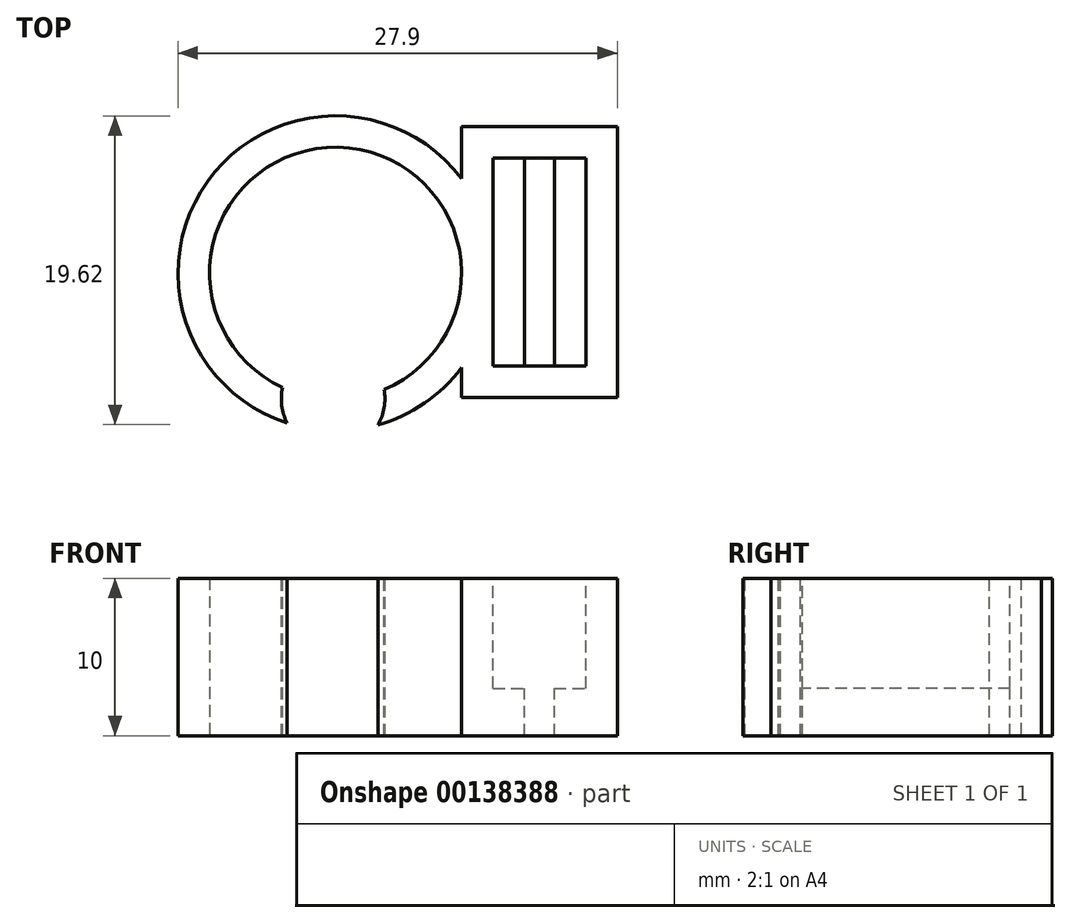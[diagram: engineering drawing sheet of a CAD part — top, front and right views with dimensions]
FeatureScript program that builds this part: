
annotation { "Feature Type Name" : "Feature", "Feature Type Description" : "" }
export const myFeature = defineFeature(function(context is Context, id is Id, definition is map)
    precondition{}
    {
        {
            var Q0;
            Q0=qCreatedBy(makeId("Top.planeOp"),FACE);
            var sketch = newSketch(context, id + "F0", { "sketchPlane" : qUnion([Q0])});
            skCircle(sketch, "E0", {"center": v(-52.4, 40.08) * mm, "radius": 8 * mm});
            skCircle(sketch, "E1", {"center": v(-52.4, 40.08) * mm, "radius": 10 * mm});
            skSolve(sketch);
        }
        {
            var Q0;
            Q0=makeQuery(id+"F0.imprint","IMPRINT",FACE,{"disambiguationData":[TD([[makeQuery(id+"F0.imprint","IMPRINT",EDGE,{"derivedFrom":sQuery(id+"F0.wireOp",EDGE,"E0")}),-1.0]])]});
            extrude(context, id + "F1", {"entities" : qUnion([Q0]), "depth" : 10 * mm});
        }
        {
            var Q0;
            Q0=makeQuery(id+"F1.opExtrude","CAP_FACE",FACE,{"disambiguationData":[OSD([sQuery(id+"F0.wireOp",EDGE,"E0"),sQuery(id+"F0.wireOp",EDGE,"E1")])],"isStart":false});
            var sketch = newSketch(context, id + "F2", { "sketchPlane" : qUnion([Q0])});
            skCircle(sketch, "E2", {"center": v(-52.56, 32.08) * mm, "radius": 3.29 * mm});
            skSolve(sketch);
        }
        {
            var Q0;
            {var subQ0=sQuery(id+"F2.wireOp",EDGE,"E2");var subQ1=makeQuery(id+"F1.opExtrude","CAP_EDGE",EDGE,{"disambiguationData":[OSD([sQuery(id+"F0.wireOp",EDGE,"E1")])],"isStart":false});var subQ2=makeQuery(id+"F2.imprint","INTERSECT",VERTEX,{"disambiguationData":[OD(0.0)],"derivedFrom":[subQ1,subQ0]});Q0=makeQuery(id+"F2.imprint","IMPRINT",FACE,{"disambiguationData":[TD([[makeQuery(id+"F2.imprint","IMPRINT",EDGE,{"disambiguationData":[TD([[subQ2,1.0]])],"derivedFrom":subQ0}),1.0]])]});}
            extrude(context, id + "F3", {"entities" : qUnion([Q0]), "operationType" : NewBodyOperationType.REMOVE, "endBound" : BoundingType.THROUGH_ALL, "oppositeDirection" : true, "depth" : 25 * mm});
        }
        {
            var Q0;
            Q0=makeQuery(id+"F1.opExtrude","CAP_FACE",FACE,{"disambiguationData":[OSD([sQuery(id+"F0.wireOp",EDGE,"E0"),sQuery(id+"F0.wireOp",EDGE,"E1")])],"isStart":false});
            var sketch = newSketch(context, id + "F4", { "sketchPlane" : qUnion([Q0])});
            skLineSegment(sketch, "E3.bottom", {"start": v(-44.4, 49.4) * mm, "end": v(-34.5, 49.4) * mm});
            skLineSegment(sketch, "E3.top", {"start": v(-44.4, 32.2) * mm, "end": v(-34.5, 32.2) * mm});
            skLineSegment(sketch, "E3.left", {"start": v(-44.4, 49.4) * mm, "end": v(-44.4, 32.2) * mm});
            skLineSegment(sketch, "E3.right", {"start": v(-34.5, 49.4) * mm, "end": v(-34.5, 32.2) * mm});
            skSolve(sketch);
        }
        {
            var Q0;
            {var subQ0=sQuery(id+"F4.wireOp",EDGE,"E3.left");var subQ1=makeQuery(id+"F1.opExtrude","CAP_EDGE",EDGE,{"disambiguationData":[OSD([sQuery(id+"F0.wireOp",EDGE,"E1")])],"isStart":false});var subQ2=makeQuery(id+"F4.imprint","INTERSECT",VERTEX,{"disambiguationData":[OD(0.0)],"derivedFrom":[subQ1,subQ0]});Q0=makeQuery(id+"F4.imprint","IMPRINT",FACE,{"disambiguationData":[TD([[makeQuery(id+"F4.imprint","IMPRINT",EDGE,{"disambiguationData":[TD([[subQ2,-1.0]])],"derivedFrom":subQ0}),1.0]])]});}
            extrude(context, id + "F5", {"entities" : qUnion([Q0]), "operationType" : NewBodyOperationType.REMOVE, "endBound" : BoundingType.THROUGH_ALL, "oppositeDirection" : true, "depth" : 25 * mm});
        }
        {
            var Q0;
            Q0 = qSketchRegion(id + "F4", true);
            extrude(context, id + "F6", {"entities" : qUnion([Q0]), "oppositeDirection" : true, "depth" : 7 * mm});
        }
        {
            var Q0;
            Q0=makeQuery(id+"F6.opExtrude","CAP_FACE",FACE,{"disambiguationData":[OSD([sQuery(id+"F4.wireOp",EDGE,"E3.bottom"),sQuery(id+"F4.wireOp",EDGE,"E3.top"),sQuery(id+"F4.wireOp",EDGE,"E3.left"),sQuery(id+"F4.wireOp",EDGE,"E3.right")])],"isStart":true});
            var sketch = newSketch(context, id + "F7", { "sketchPlane" : qUnion([Q0])});
            skLineSegment(sketch, "E4.bottom", {"start": v(-42.4, 47.4) * mm, "end": v(-36.5, 47.4) * mm});
            skLineSegment(sketch, "E4.top", {"start": v(-42.4, 34.2) * mm, "end": v(-36.5, 34.2) * mm});
            skLineSegment(sketch, "E4.left", {"start": v(-42.4, 47.4) * mm, "end": v(-42.4, 34.2) * mm});
            skLineSegment(sketch, "E4.right", {"start": v(-36.5, 47.4) * mm, "end": v(-36.5, 34.2) * mm});
            skSolve(sketch);
        }
        {
            var Q0;
            Q0=makeQuery(id+"F7.imprint","IMPRINT",FACE,{"disambiguationData":[TD([[makeQuery(id+"F7.imprint","IMPRINT",EDGE,{"derivedFrom":sQuery(id+"F7.wireOp",EDGE,"E4.bottom")}),-1.0]])]});
            var Q1;
            Q1 = qSketchRegion(id + "F9", true);
            extrude(context, id + "F8", {"entities" : qUnion([Q0, Q1]), "operationType" : NewBodyOperationType.REMOVE, "oppositeDirection" : true, "depth" : 25 * mm});
        }
        {
            var Q0;
            Q0=makeQuery(id+"F6.opExtrude","CAP_FACE",FACE,{"disambiguationData":[OSD([sQuery(id+"F4.wireOp",EDGE,"E3.bottom"),sQuery(id+"F4.wireOp",EDGE,"E3.top"),sQuery(id+"F4.wireOp",EDGE,"E3.left"),sQuery(id+"F4.wireOp",EDGE,"E3.right")])],"isStart":false});
            var sketch = newSketch(context, id + "F9", { "sketchPlane" : qUnion([Q0])});
            skLineSegment(sketch, "E5.bottom", {"start": v(-42.4, -34.2) * mm, "end": v(-40.4, -34.2) * mm});
            skLineSegment(sketch, "E5.top", {"start": v(-42.4, -47.4) * mm, "end": v(-40.4, -47.4) * mm});
            skLineSegment(sketch, "E5.left", {"start": v(-42.4, -34.2) * mm, "end": v(-42.4, -47.4) * mm});
            skLineSegment(sketch, "E5.right", {"start": v(-40.4, -34.2) * mm, "end": v(-40.4, -47.4) * mm});
            skLineSegment(sketch, "E6.bottom", {"start": v(-38.5, -34.2) * mm, "end": v(-36.5, -34.2) * mm});
            skLineSegment(sketch, "E6.top", {"start": v(-38.5, -47.4) * mm, "end": v(-36.5, -47.4) * mm});
            skLineSegment(sketch, "E6.left", {"start": v(-38.5, -34.2) * mm, "end": v(-38.5, -47.4) * mm});
            skLineSegment(sketch, "E6.right", {"start": v(-36.5, -34.2) * mm, "end": v(-36.5, -47.4) * mm});
            skLineSegment(sketch, "E7.bottom", {"start": v(-44.4, -32.2) * mm, "end": v(-34.5, -32.2) * mm});
            skLineSegment(sketch, "E7.top", {"start": v(-44.4, -49.4) * mm, "end": v(-34.5, -49.4) * mm});
            skLineSegment(sketch, "E7.left", {"start": v(-44.4, -32.2) * mm, "end": v(-44.4, -49.4) * mm});
            skLineSegment(sketch, "E7.right", {"start": v(-34.5, -32.2) * mm, "end": v(-34.5, -49.4) * mm});
            skSolve(sketch);
        }
        {
            var Q0;
            {var subQ1=sQuery(id+"F9.wireOp",EDGE,"E5.bottom");Q0=makeQuery(id+"F9.imprint","IMPRINT",FACE,{"disambiguationData":[TD([[makeQuery(id+"F9.imprint","IMPRINT",EDGE,{"derivedFrom":subQ1}),1.0]])]});}
            var Q1;
            Q1=makeQuery(id+"F9.imprint","IMPRINT",FACE,{"disambiguationData":[TD([[makeQuery(id+"F9.imprint","IMPRINT",EDGE,{"derivedFrom":sQuery(id+"F9.wireOp",EDGE,"E5.bottom")}),-1.0]])]});
            var Q2;
            Q2=makeQuery(id+"F9.imprint","IMPRINT",FACE,{"disambiguationData":[TD([[makeQuery(id+"F9.imprint","IMPRINT",EDGE,{"derivedFrom":sQuery(id+"F9.wireOp",EDGE,"E6.bottom")}),-1.0]])]});
            extrude(context, id + "F10", {"entities" : qUnion([Q0, Q1, Q2]), "operationType" : NewBodyOperationType.ADD, "depth" : 3 * mm});
        }
    });
